# Revit family: Differenzdruckregler mit Durchflussbegrenzung 4012 LF
name_source: partatom
category: Rohrzubehör
units: mm (PartAtom-declared; Revit-internal decimal feet)

## family parameters
Arbeitsebenenbasiert = Nein
Beim Laden mit Abzugskörper schneiden = Nein
Bemaßung runder Anschluss = Durchmesser verwenden
Gemeinsam genutzt = Nein
Immer vertikal = Ja
OmniClass-Nummer = 23.65.55.14
OmniClass-Titel = Valves for Liquid Services
Teiletyp = Unterbricht

## types (1)
- LF
    Antrieb-Anschlussgewinde = M28 x 1,5
    Anwendung = HERZ-Differenzdruckregler VS-TS ist für Heiz- und Kühlanwendungen vorgesehen - Radiator- oder Fußbodenheizungssysteme.
Die Konstruktion dieses Ventils vereint in einem Ventil vier Funktionalitäten:
Differenzdruckregler, Strangregulierventil, Zonenventil, Absperrventil.
    Bauschutzkappe = Kunststoff
    D01 = 10 mm  [stored 0.0328084 ft]
    D02 = 11 mm  [stored 0.0360892 ft]
    D03 = 15 mm  [stored 0.0492126 ft]
    D04 = 19.5 mm  [stored 0.0639764 ft]
    D05 = 22 mm  [stored 0.0721785 ft]
    D06 = 16.8 mm  [stored 0.0551181 ft]
    D07 = 8.6 mm
    D08 = 5.3 mm  [stored 0.0173885 ft]
    D09 = 13.9 mm  [stored 0.0456037 ft]
    D10 = 12.75 mm
    Druckfeder = Federstahl
    Durchfluss bei Einstellung 100% = 0.0 L/s
    H01 = 31 mm
    H02 = 54.1 mm
    H03 = 4.8 mm  [stored 0.015748 ft]
    H04 = 9.1 mm  [stored 0.0298556 ft]
    H05 = 34.8 mm
    H06 = 26.4 mm
    H07 = 3.3 mm  [stored 0.0108268 ft]
    H08 = 10.2 mm  [stored 0.0334646 ft]
    H09 = 16.2 mm  [stored 0.0531496 ft]
    H10 = 9 mm  [stored 0.0295276 ft]
    H11 = 2.5 mm  [stored 0.0082021 ft]
    H12 = 3.2 mm  [stored 0.0104987 ft]
    H13 = 23.1 mm  [stored 0.0757874 ft]
    H14 = 2 mm  [stored 0.00656168 ft]
    H15 = 22.5 mm  [stored 0.0738189 ft]
    H16 = 9 mm  [stored 0.0295276 ft]
    H17 = 2 mm  [stored 0.00656168 ft]
    H18 = 44.5 mm
    Hersteller = HERZ Armaturen Ges.m.b.H
    Hub = 4 mm
    L01 = 41 mm
    L02 = 8 mm  [stored 0.0262467 ft]
    L03 = 23.7 mm  [stored 0.0777559 ft]
    L04 = 5.15 mm
    L05 = 16.5 mm  [stored 0.0541339 ft]
    L06 = 7.5 mm  [stored 0.0246063 ft]
    L07 = 12.5 mm  [stored 0.0410105 ft]
    L08 = 13 mm
    L09 = 6.9 mm  [stored 0.0226378 ft]
    L10 = 34 mm
    Max. Betriebsdruck = 1600000.0 Pa
    Max. Betriebstemperatur = 130 °C
    Max. Differenzdruck = 400000.0 Pa
    Max. Differenzdruck ohne Last = 25000.0 Pa
    Medium = Wasserbeschaffenheit gemäß ÖNORM H5195 und VDI 2035.
Die Verwendung von Ethylen- und Propylenglykol ist im Mischungsverhältnis 25 - 50 Vol.- % zulässig.
    Membrane = EPDM
    Membrangehäuse = Messing CW602N
    Min. Betriebstemperatur (Frostschutz) = -20 °C
    Min. Betriebstemperatur (reines Wasser) = 2 °C
    Min. Differenzdruck = 10000.0 Pa
    Nennweite = 15 mm  [stored 0.0492126 ft]
    O-Ringe = EPDM
    Regelbereich = 10% - 100%
    S01 = 10 mm  [stored 0.0328084 ft]
    S02 = 30 mm
    S03 = 37.5 mm
    SB02 = 44 mm
    SCRNCODE = 05;03;02
    SCRNSEQ = ARM;ARM_TYP="DIFR";2
    SH01 = 21 mm
    SH02 = 33 mm
    Stift = Edelstahl 14301
    T00 = 14.4 mm  [stored 0.0472441 ft]
    T01 = 3.4 mm  [stored 0.0111549 ft]
    T02 = 2.5 mm  [stored 0.0082021 ft]
    T03 = 4.8 mm  [stored 0.015748 ft]
    T04 = 1 mm  [stored 0.00328084 ft]
    T05 = 1.2 mm  [stored 0.00393701 ft]
    T06 = 3.9 mm  [stored 0.0127953 ft]
    T07 = 4.9 mm  [stored 0.0160761 ft]
    T08 = 13 mm
    T09 = 6.9 mm  [stored 0.0226378 ft]
    URL = www.herz-armaturen.at
    VRD01 = 18.5 mm  [stored 0.0606955 ft]
    VRD02 = 16.2 mm  [stored 0.0531496 ft]
    VRD03 = 12 mm  [stored 0.0393701 ft]
    VRG03 = 7.5 mm  [stored 0.0246063 ft]
    VRL01 = 30 mm
    VRL02 = 18 mm  [stored 0.0590551 ft]
    VRL03 = 12 mm  [stored 0.0393701 ft]
    VRL04 = 8 mm  [stored 0.0262467 ft]
    Ventilgehäuse = DZR Messing CC770S
    Vorgabe-Ansicht = 0 mm  [stored 0 ft]

note: [stored X ft] marks values corroborated as IEEE doubles in the binary element streams (Revit-internal decimal feet)
